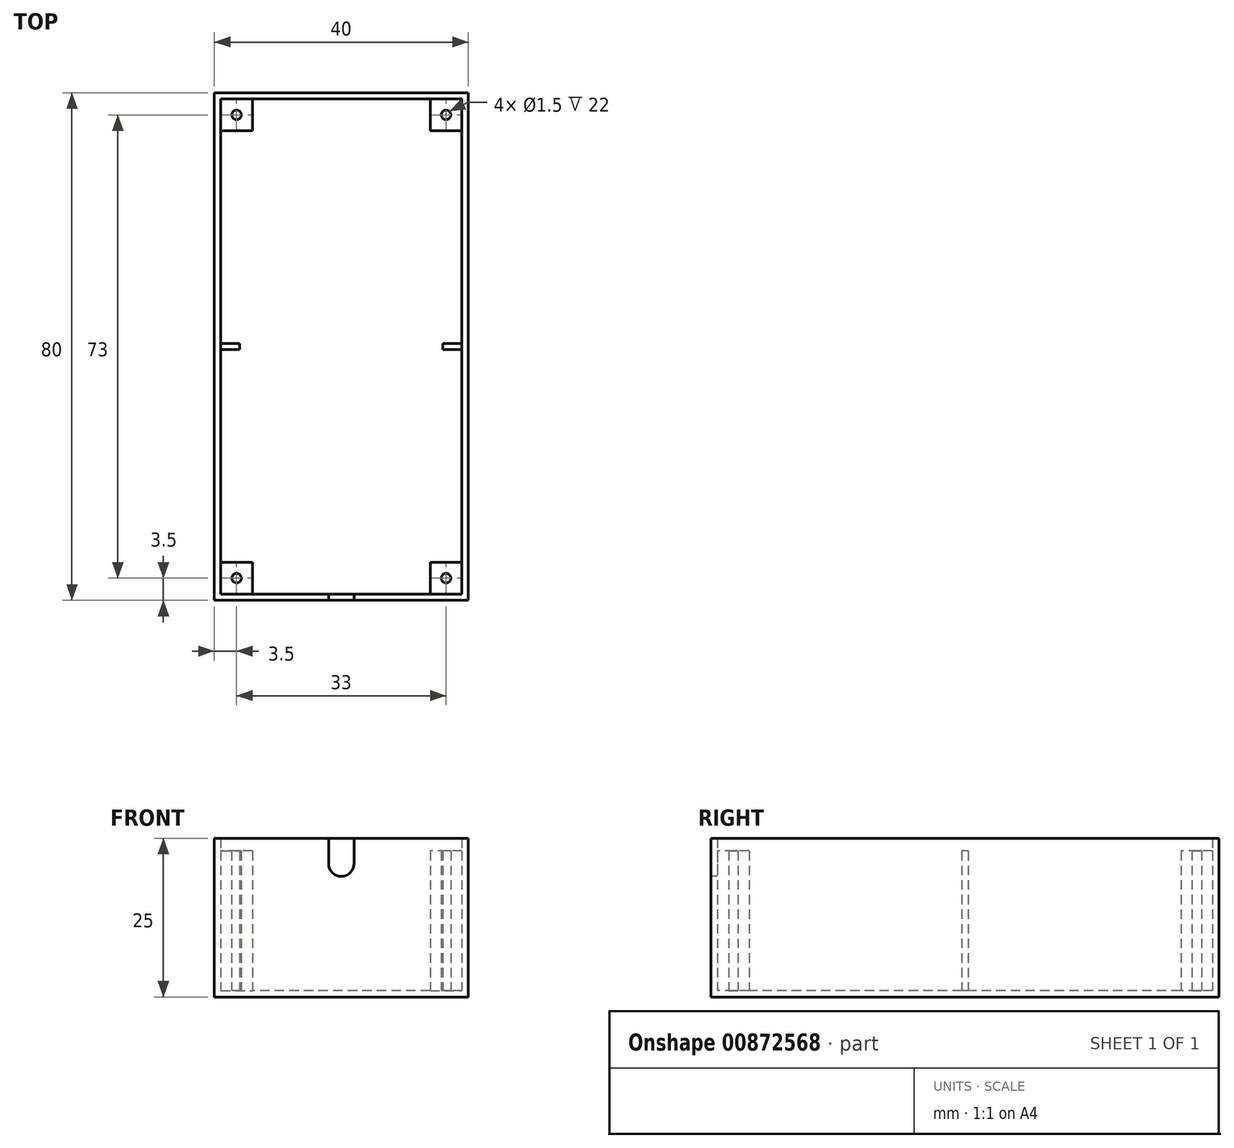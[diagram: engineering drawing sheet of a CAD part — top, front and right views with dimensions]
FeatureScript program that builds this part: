
annotation { "Feature Type Name" : "Feature", "Feature Type Description" : "" }
export const myFeature = defineFeature(function(context is Context, id is Id, definition is map)
    precondition{}
    {
        {
            var Q0;
            Q0=qCreatedBy(makeId("Top.planeOp"),FACE);
            var sketch = newSketch(context, id + "F0", { "sketchPlane" : qUnion([Q0])});
            skLineSegment(sketch, "E0.bottom", {"start": v(20, 40) * mm, "end": v(-20, 40) * mm});
            skLineSegment(sketch, "E0.top", {"start": v(20, -40) * mm, "end": v(-20, -40) * mm});
            skLineSegment(sketch, "E0.left", {"start": v(20, 40) * mm, "end": v(20, -40) * mm});
            skLineSegment(sketch, "E0.right", {"start": v(-20, 40) * mm, "end": v(-20, -40) * mm});
            skPoint(sketch, "E0.middle", {"position": v(0, 0) * mm});
            skSolve(sketch);
        }
        {
            var Q0;
            Q0 = qSketchRegion(id + "F0", true);
            extrude(context, id + "F1", {"entities" : qUnion([Q0]), "depth" : 25 * mm, "offsetDistance" : 25 * mm});
        }
        {
            var Q0;
            Q0=makeQuery(id+"F1.opExtrude","CAP_FACE",FACE,{"disambiguationData":[OSD([sQuery(id+"F0.wireOp",EDGE,"E0.bottom"),sQuery(id+"F0.wireOp",EDGE,"E0.top"),sQuery(id+"F0.wireOp",EDGE,"E0.left"),sQuery(id+"F0.wireOp",EDGE,"E0.right")])],"isStart":false});
            shell(context, id + "F2", {"entities" : qUnion([Q0]), "thickness" : 1 * mm});
        }
        {
            var Q0;
            Q0=makeQuery(id+"F2.opShell","OFFSET_FACE",FACE,{"disambiguationData":[OSD([sQuery(id+"F0.wireOp",EDGE,"E0.bottom"),sQuery(id+"F0.wireOp",EDGE,"E0.top"),sQuery(id+"F0.wireOp",EDGE,"E0.left"),sQuery(id+"F0.wireOp",EDGE,"E0.right")])]});
            var sketch = newSketch(context, id + "F3", { "sketchPlane" : qUnion([Q0])});
            skLineSegment(sketch, "E1.bottom", {"start": v(-19, 39) * mm, "end": v(-14, 39) * mm});
            skLineSegment(sketch, "E1.top", {"start": v(-19, 34) * mm, "end": v(-14, 34) * mm});
            skLineSegment(sketch, "E1.left", {"start": v(-19, 39) * mm, "end": v(-19, 34) * mm});
            skLineSegment(sketch, "E1.right", {"start": v(-14, 39) * mm, "end": v(-14, 34) * mm});
            skCircle(sketch, "E2", {"center": v(-16.5, 36.5) * mm, "radius": 0.75 * mm});
            skLineSegment(sketch, "E3.0.1.0", {"start": v(-19, -39) * mm, "end": v(-14, -39) * mm});
            skLineSegment(sketch, "E3.0.1.1", {"start": v(-19, -34) * mm, "end": v(-14, -34) * mm});
            skLineSegment(sketch, "E3.0.1.2", {"start": v(-19, -34) * mm, "end": v(-19, -39) * mm});
            skLineSegment(sketch, "E3.0.1.3", {"start": v(-14, -34) * mm, "end": v(-14, -39) * mm});
            skCircle(sketch, "E3.0.1.4", {"center": v(-16.5, -36.5) * mm, "radius": 0.75 * mm});
            skLineSegment(sketch, "E3.1.0.0", {"start": v(14, 34) * mm, "end": v(19, 34) * mm});
            skLineSegment(sketch, "E3.1.0.1", {"start": v(14, 39) * mm, "end": v(19, 39) * mm});
            skLineSegment(sketch, "E3.1.0.2", {"start": v(14, 39) * mm, "end": v(14, 34) * mm});
            skLineSegment(sketch, "E3.1.0.3", {"start": v(19, 39) * mm, "end": v(19, 34) * mm});
            skCircle(sketch, "E3.1.0.4", {"center": v(16.5, 36.5) * mm, "radius": 0.75 * mm});
            skLineSegment(sketch, "E3.1.1.0", {"start": v(14, -39) * mm, "end": v(19, -39) * mm});
            skLineSegment(sketch, "E3.1.1.1", {"start": v(14, -34) * mm, "end": v(19, -34) * mm});
            skLineSegment(sketch, "E3.1.1.2", {"start": v(14, -34) * mm, "end": v(14, -39) * mm});
            skLineSegment(sketch, "E3.1.1.3", {"start": v(19, -34) * mm, "end": v(19, -39) * mm});
            skCircle(sketch, "E3.1.1.4", {"center": v(16.5, -36.5) * mm, "radius": 0.75 * mm});
            skLineSegment(sketch, "E3.direction1", {"start": v(-19, 34) * mm, "end": v(14, 34) * mm, "construction": true});
            skLineSegment(sketch, "E3.direction2", {"start": v(-19, 34) * mm, "end": v(-19, -39) * mm, "construction": true});
            skLineSegment(sketch, "E4.bottom", {"start": v(-19, -9.5) * mm, "end": v(-17, -9.5) * mm, "construction": true});
            skLineSegment(sketch, "E4.top", {"start": v(-19, 9.5) * mm, "end": v(-17, 9.5) * mm, "construction": true});
            skLineSegment(sketch, "E4.left", {"start": v(-19, 9.5) * mm, "end": v(-19, -9.5) * mm, "construction": true});
            skLineSegment(sketch, "E5.bottom", {"start": v(-19, 0.5) * mm, "end": v(-16, 0.5) * mm});
            skLineSegment(sketch, "E5.top", {"start": v(-19, -0.5) * mm, "end": v(-16, -0.5) * mm});
            skLineSegment(sketch, "E5.left", {"start": v(-19, 0.5) * mm, "end": v(-19, -0.5) * mm});
            skLineSegment(sketch, "E5.right", {"start": v(-16, 0.5) * mm, "end": v(-16, -0.5) * mm});
            skLineSegment(sketch, "E6.bottom", {"start": v(19, 0.5) * mm, "end": v(16, 0.5) * mm});
            skLineSegment(sketch, "E6.top", {"start": v(19, -0.5) * mm, "end": v(16, -0.5) * mm});
            skLineSegment(sketch, "E6.left", {"start": v(19, 0.5) * mm, "end": v(19, -0.5) * mm});
            skLineSegment(sketch, "E6.right", {"start": v(16, 0.5) * mm, "end": v(16, -0.5) * mm});
            skSolve(sketch);
        }
        {
            var Q0;
            Q0 = qSketchRegion(id + "F3", true);
            extrude(context, id + "F4", {"entities" : qUnion([Q0]), "operationType" : NewBodyOperationType.ADD, "depth" : 22 * mm, "offsetDistance" : 25 * mm});
        }
        {
            var Q0;
            Q0=makeQuery(id+"F1.opExtrude","SWEPT_FACE",FACE,{"disambiguationData":[OSD([sQuery(id+"F0.wireOp",EDGE,"E0.top")])]});
            var sketch = newSketch(context, id + "F5", { "sketchPlane" : qUnion([Q0])});
            skLineSegment(sketch, "E7.bottom", {"start": v(-2, 25) * mm, "end": v(2, 25) * mm});
            skLineSegment(sketch, "E7.left", {"start": v(-2, 25) * mm, "end": v(-2, 21) * mm});
            skLineSegment(sketch, "E7.right", {"start": v(2, 25) * mm, "end": v(2, 21) * mm});
            skArc(sketch, "E8", {"start": v(-2, 21) * mm, "mid": v(0, 19) * mm, "end": v(2, 21) * mm});
            skPoint(sketch, "E8.first.point", {"position": v(-2, 21) * mm});
            skPoint(sketch, "E8.second.point", {"position": v(0, 19) * mm});
            skPoint(sketch, "E8.third.point", {"position": v(2, 21) * mm});
            skSolve(sketch);
        }
        {
            var Q0;
            Q0 = qSketchRegion(id + "F5", true);
            extrude(context, id + "F6", {"entities" : qUnion([Q0]), "operationType" : NewBodyOperationType.REMOVE, "oppositeDirection" : true, "depth" : 25 * mm, "offsetDistance" : 25 * mm});
        }
    });
